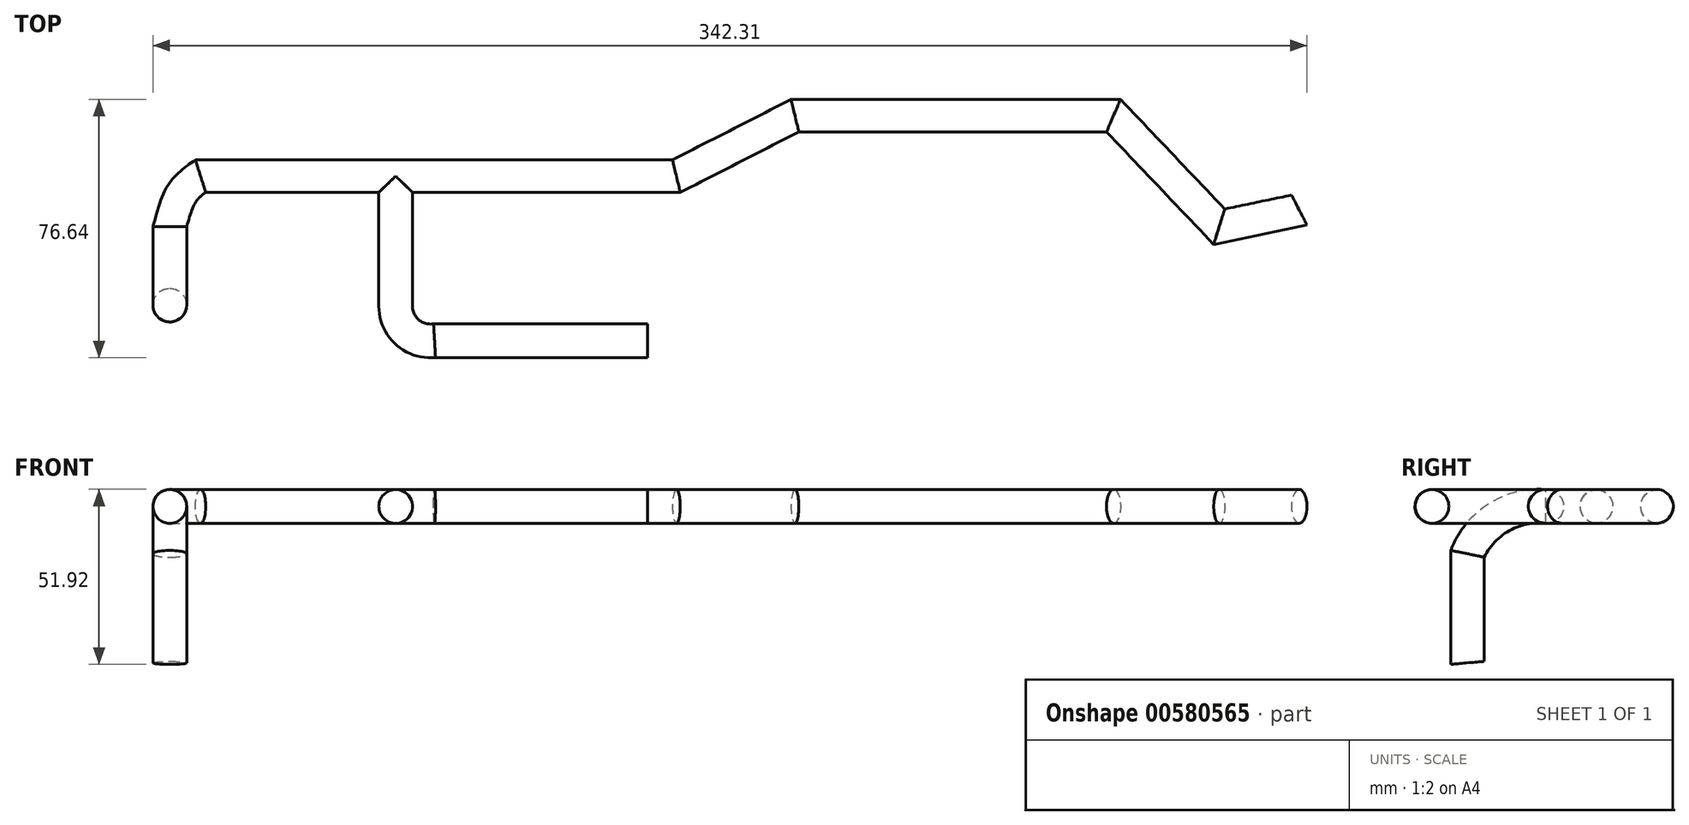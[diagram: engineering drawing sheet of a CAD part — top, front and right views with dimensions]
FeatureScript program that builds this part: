
annotation { "Feature Type Name" : "Feature", "Feature Type Description" : "" }
export const myFeature = defineFeature(function(context is Context, id is Id, definition is map)
    precondition{}
    {
        {
            var Q0;
            Q0=qCreatedBy(makeId("Top.planeOp"),FACE);
            var sketch = newSketch(context, id + "F0", { "sketchPlane" : qUnion([Q0])});
            skFitSpline(sketch, "E0", {"points": [v(-57.88, 15) * mm, v(-61.17, 12.4) * mm, v(-64.08, 8.57) * mm, v(-67, 0) * mm], "startDerivative": vector(-12.03, -8.58) * mm, "endDerivative": vector(-6.38, -22.78) * mm});
            skLineSegment(sketch, "E1", {"start": v(-57.88, 15) * mm, "end": v(83.25, 15) * mm});
            skLineSegment(sketch, "E2", {"start": v(83.25, 15) * mm, "end": v(118.42, 32.94) * mm});
            skLineSegment(sketch, "E3", {"start": v(118.42, 32.94) * mm, "end": v(212.92, 32.94) * mm});
            skLineSegment(sketch, "E4", {"start": v(212.92, 32.94) * mm, "end": v(244.28, 0) * mm});
            skLineSegment(sketch, "E5", {"start": v(244.28, 0) * mm, "end": v(268.01, 4.93) * mm});
            skSolve(sketch);
        }
        {
            var Q0;
            Q0=qCreatedBy(makeId("Front.planeOp"),FACE);
            var sketch = newSketch(context, id + "F1", { "sketchPlane" : qUnion([Q0])});
            skCircle(sketch, "E6", {"center": v(-67, 0) * mm, "radius": 5 * mm});
            skSolve(sketch);
        }
        {
            var Q0;
            Q0 = qSketchRegion(id + "F1", true);
            var Q1;
            Q1 = qConstructionFilter(qBodyType(qCreatedBy(id + "F0" ,EDGE), BodyType.WIRE), ConstructionObject.NO);
            sweep(context, id + "F2", {"profiles" : qUnion([Q0]), "path" : qUnion([Q1])});
        }
        {
            var Q0;
            Q0=qCreatedBy(makeId("Top.planeOp"),FACE);
            var sketch = newSketch(context, id + "F3", { "sketchPlane" : qUnion([Q0])});
            skLineSegment(sketch, "E7", {"start": v(0, 15) * mm, "end": v(0, -23.6) * mm});
            skLineSegment(sketch, "E8", {"start": v(11.53, -33.8) * mm, "end": v(74.73, -33.8) * mm});
            skArc(sketch, "E9", {"start": v(0, -23.6) * mm, "mid": v(3.47, -31.3) * mm, "end": v(11.53, -33.8) * mm});
            skSolve(sketch);
        }
        {
            var Q0;
            Q0=qCreatedBy(makeId("Front.planeOp"),FACE);
            cPlane(context, id + "F4", {"entities" : qUnion([Q0]), "cplaneType" : CPlaneType.OFFSET, "offset" : 15 * mm, "oppositeDirection" : true, "width" : 150 * mm, "height" : 150 * mm});
        }
        {
            var Q0;
            Q0=qCreatedBy(id+"F4.planeOp",FACE);
            var sketch = newSketch(context, id + "F5", { "sketchPlane" : qUnion([Q0])});
            skCircle(sketch, "E10", {"center": v(0, 0) * mm, "radius": 5 * mm});
            skSolve(sketch);
        }
        {
            var Q0;
            Q0 = qSketchRegion(id + "F5", true);
            var Q1;
            Q1 = qConstructionFilter(qBodyType(qCreatedBy(id + "F3" ,EDGE), BodyType.WIRE), ConstructionObject.NO);
            sweep(context, id + "F6", {"operationType" : NewBodyOperationType.ADD, "profiles" : qUnion([Q0]), "path" : qUnion([Q1])});
        }
        {
            var Q0;
            Q0=qCreatedBy(makeId("Right.planeOp"),FACE);
            cPlane(context, id + "F7", {"entities" : qUnion([Q0]), "cplaneType" : CPlaneType.OFFSET, "offset" : 67 * mm, "oppositeDirection" : true, "width" : 150 * mm, "height" : 150 * mm});
        }
        {
            var Q0;
            Q0=qCreatedBy(id+"F7.planeOp",FACE);
            var sketch = newSketch(context, id + "F8", { "sketchPlane" : qUnion([Q0])});
            skArc(sketch, "E11", {"start": v(0, 0) * mm, "mid": v(-13.93, -3.21) * mm, "end": v(-23.27, -14.04) * mm});
            skLineSegment(sketch, "E12", {"start": v(-23.27, -14.04) * mm, "end": v(-23.27, -46.4) * mm});
            skSolve(sketch);
        }
        {
            var Q0;
            Q0 = qSketchRegion(id + "F1", true);
            var Q1;
            Q1 = qConstructionFilter(qBodyType(qCreatedBy(id + "F8" ,EDGE), BodyType.WIRE), ConstructionObject.NO);
            sweep(context, id + "F9", {"operationType" : NewBodyOperationType.ADD, "profiles" : qUnion([Q0]), "path" : qUnion([Q1])});
        }
    });
